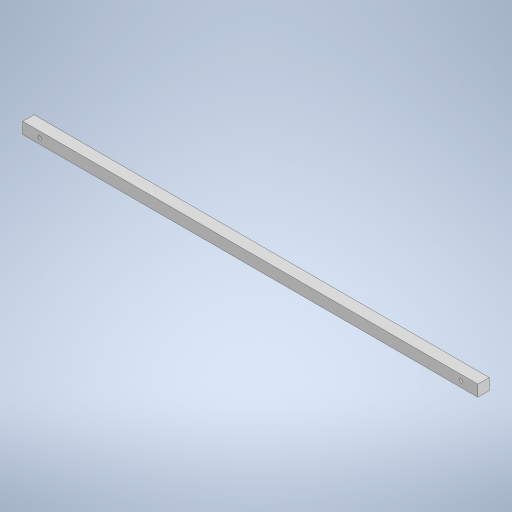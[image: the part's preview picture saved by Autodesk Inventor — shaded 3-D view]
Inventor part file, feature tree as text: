
AUTODESK INVENTOR PART (.ipt)
format: ipt  version: 2023 (Build 270158000, 158)  size: 242,688 bytes
history: native  units: mm
features: sketch x2, other x1, extrude x1, hole x1
ambient origin geometry x8: Origin, YZ Plane, XZ Plane, XY Plane, X Axis, Y Axis, Z Axis, Center Point
bodies: Body1 (feature_tree)
feature tree (5):
  other  "ソリッド1"
  extrude  "押し出し1"  Depth=400.0mm
  hole  "穴2"  [1 undecoded]
  sketch  "スケッチ1"
  sketch  "スケッチ5"
note: 1 required parameter value undecoded (feature->parameter linkage not recoverable at this tier; creation-order binding heuristic only, values carry confidence <= 0.55)
